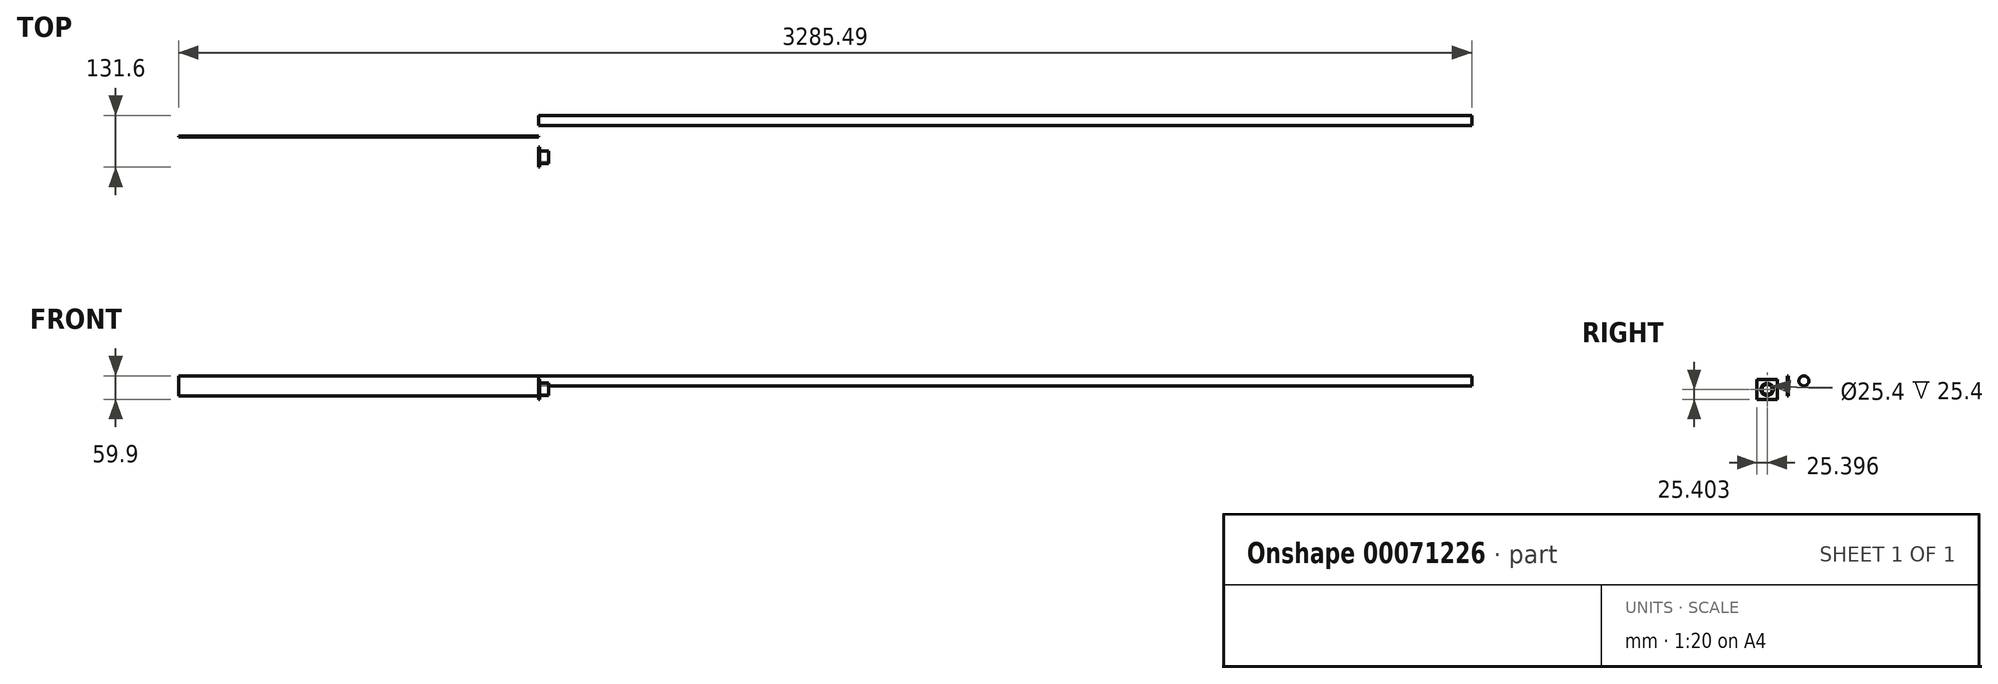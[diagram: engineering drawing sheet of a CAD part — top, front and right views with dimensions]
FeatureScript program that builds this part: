
annotation { "Feature Type Name" : "Feature", "Feature Type Description" : "" }
export const myFeature = defineFeature(function(context is Context, id is Id, definition is map)
    precondition{}
    {
        {
            var Q0;
            Q0=qCreatedBy(makeId("Front.planeOp"),FACE);
            var sketch = newSketch(context, id + "F0", { "sketchPlane" : qUnion([Q0])});
            skLineSegment(sketch, "E0.bottom", {"start": v(-914.4, 50.8) * mm, "end": v(0, 50.8) * mm});
            skLineSegment(sketch, "E0.top", {"start": v(-914.4, 0) * mm, "end": v(0, 0) * mm});
            skLineSegment(sketch, "E0.left", {"start": v(-914.4, 50.8) * mm, "end": v(-914.4, 0) * mm});
            skLineSegment(sketch, "E0.right", {"start": v(0, 50.8) * mm, "end": v(0, 0) * mm});
            skSolve(sketch);
        }
        {
            var Q0;
            Q0=makeQuery(id+"F0.imprint","IMPRINT",FACE,{"disambiguationData":[TD([[makeQuery(id+"F0.imprint","IMPRINT",EDGE,{"derivedFrom":sQuery(id+"F0.wireOp",EDGE,"E0.bottom")}),-1.0]])]});
            extrude(context, id + "F1", {"entities" : qUnion([Q0]), "depth" : 3.17 * mm});
        }
        {
            var Q0;
            Q0=qCreatedBy(makeId("Right.planeOp"),FACE);
            var sketch = newSketch(context, id + "F2", { "sketchPlane" : qUnion([Q0])});
            skLineSegment(sketch, "E1.bottom", {"start": v(-28.6, -8.74) * mm, "end": v(-79.4, -8.74) * mm});
            skLineSegment(sketch, "E1.top", {"start": v(-28.6, 42.06) * mm, "end": v(-79.4, 42.06) * mm});
            skLineSegment(sketch, "E1.left", {"start": v(-28.6, -8.74) * mm, "end": v(-28.6, 42.06) * mm});
            skLineSegment(sketch, "E1.right", {"start": v(-79.4, -8.74) * mm, "end": v(-79.4, 42.06) * mm});
            skCircle(sketch, "E2", {"center": v(-54, 16.66) * mm, "radius": 15.88 * mm});
            skLineSegment(sketch, "E3", {"start": v(-28.6, 42.06) * mm, "end": v(-79.4, -8.74) * mm, "construction": true});
            skCircle(sketch, "E4", {"center": v(-54, 16.66) * mm, "radius": 12.7 * mm});
            skSolve(sketch);
        }
        {
            var Q0;
            Q0=makeQuery(id+"F2.imprint","IMPRINT",FACE,{"disambiguationData":[TD([[makeQuery(id+"F2.imprint","IMPRINT",EDGE,{"derivedFrom":sQuery(id+"F2.wireOp",EDGE,"E1.bottom")}),-1.0]])]});
            extrude(context, id + "F3", {"entities" : qUnion([Q0]), "depth" : 3.17 * mm});
        }
        {
            var Q0;
            Q0=makeQuery(id+"F2.imprint","IMPRINT",FACE,{"disambiguationData":[TD([[makeQuery(id+"F2.imprint","IMPRINT",EDGE,{"derivedFrom":sQuery(id+"F2.wireOp",EDGE,"E2")}),1.0]])]});
            extrude(context, id + "F4", {"entities" : qUnion([Q0]), "operationType" : NewBodyOperationType.ADD, "depth" : 25.4 * mm});
        }
        {
            var Q0;
            Q0=qCreatedBy(makeId("Right.planeOp"),FACE);
            var sketch = newSketch(context, id + "F5", { "sketchPlane" : qUnion([Q0])});
            skCircle(sketch, "E5", {"center": v(39.5, 38.46) * mm, "radius": 12.7 * mm});
            skSolve(sketch);
        }
        {
            var Q0;
            Q0=makeQuery(id+"F5.imprint","IMPRINT",FACE,{"disambiguationData":[TD([[makeQuery(id+"F5.imprint","IMPRINT",EDGE,{"derivedFrom":sQuery(id+"F5.wireOp",EDGE,"E5")}),1.0]])]});
            extrude(context, id + "F6", {"entities" : qUnion([Q0]), "depth" : 2371.1 * mm});
        }
    });
